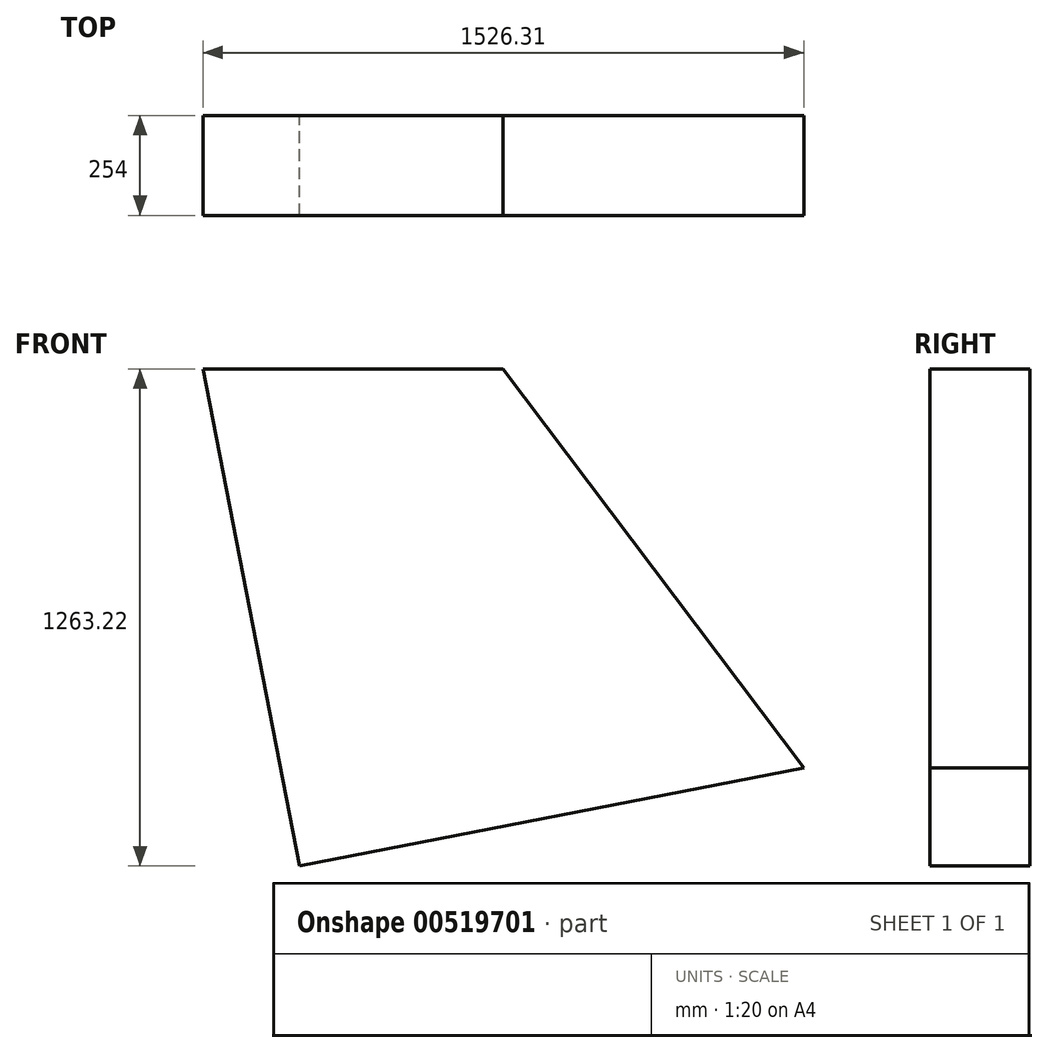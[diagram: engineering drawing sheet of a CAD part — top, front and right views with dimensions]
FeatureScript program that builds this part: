
annotation { "Feature Type Name" : "Feature", "Feature Type Description" : "" }
export const myFeature = defineFeature(function(context is Context, id is Id, definition is map)
    precondition{}
    {
        {
            var Q0;
            Q0=qCreatedBy(makeId("Front.planeOp"),FACE);
            var sketch = newSketch(context, id + "F0", { "sketchPlane" : qUnion([Q0])});
            skLineSegment(sketch, "E0", {"start": v(0, 0) * mm, "end": v(762, 0) * mm});
            skLineSegment(sketch, "E1", {"start": v(762, 0) * mm, "end": v(1526.3, -1014.27) * mm});
            skLineSegment(sketch, "E2", {"start": v(1526.3, -1014.27) * mm, "end": v(245.55, -1263.22) * mm});
            skLineSegment(sketch, "E3", {"start": v(245.55, -1263.22) * mm, "end": v(0, 0) * mm});
            skSolve(sketch);
        }
        {
            var Q0;
            Q0=makeQuery(id+"F0.imprint","IMPRINT",FACE,{"disambiguationData":[TD([[makeQuery(id+"F0.imprint","IMPRINT",EDGE,{"derivedFrom":sQuery(id+"F0.wireOp",EDGE,"E0")}),-1.0]])]});
            extrude(context, id + "F1", {"entities" : qUnion([Q0]), "depth" : 254 * mm, "offsetDistance" : 25.4 * mm});
        }
    });
